# Revit family: Клапан обратный RSK
name_source: partatom
category: Арматура воздуховодов
units: mm (PartAtom-declared; Revit-internal decimal feet)

## family parameters
Всегда вертикально = Да
На основе рабочей плоскости = Нет
Общий = Да
При загрузке вырезать с полостями = Нет
Размер круглого соединителя = Использовать диаметр
Тип детали = Вставляется

## types (6) — shared parameters
ADSK_Единица измерения = шт.
ADSK_Завод-изготовитель = Naveka
ADSK_Наименование = Клапан обратный RSK
ADSK_Примечание = https://progress-nw.ru
Материал = RAL 0000 Серый металл
zero-valued in all types: ADSK_Масса

## per-type parameters (varying)
| type | A | B | C | D |
| RSK 100 | 100 мм | 45 мм | 40 мм | 90 мм |
| RSK 125 | 125 мм | 45 мм | 40 мм | 90 мм |
| RSK 160 | 160 мм | 45 мм | 40 мм | 90 мм |
| RSK 200 | 200 мм | 45 мм | 40 мм | 90 мм |
| RSK 250 | 250 мм | 65 мм | 60 мм | 130 мм |
| RSK 315 | 315 мм | 65 мм | 65 мм | 135 мм |

note: column(s) folded — value = type name in every type: ADSK_Марка
